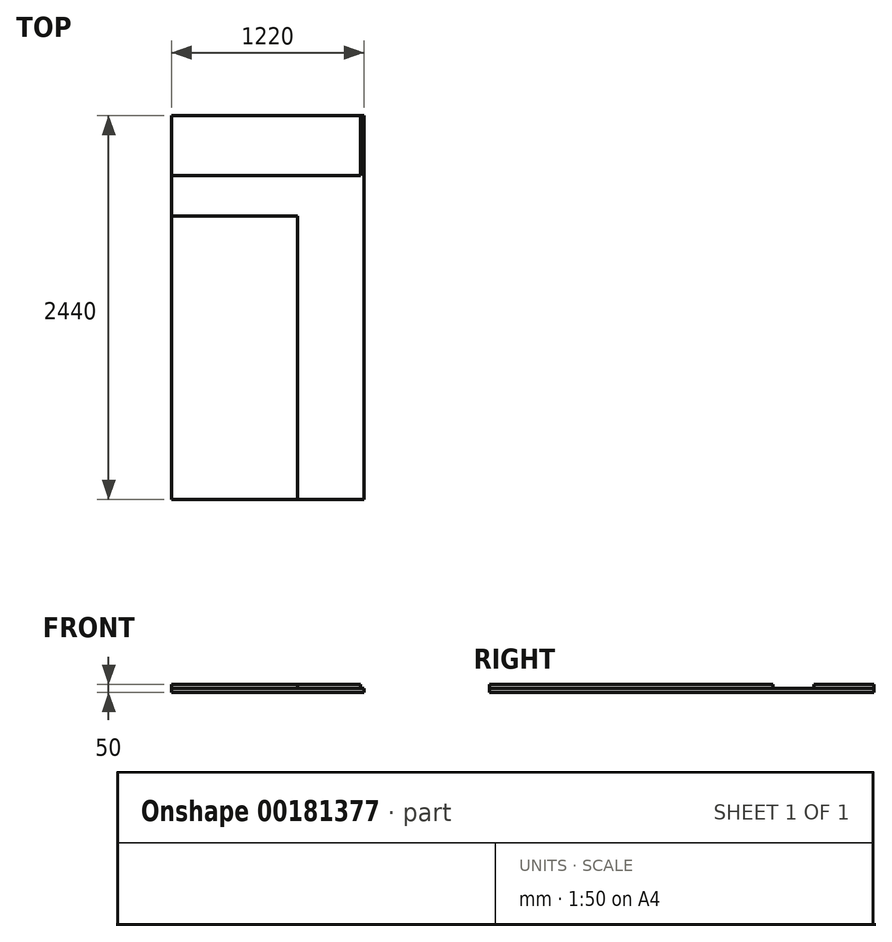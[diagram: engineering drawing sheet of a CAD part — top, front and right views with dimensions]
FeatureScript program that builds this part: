
annotation { "Feature Type Name" : "Feature", "Feature Type Description" : "" }
export const myFeature = defineFeature(function(context is Context, id is Id, definition is map)
    precondition{}
    {
        {
            var Q0;
            Q0=qCreatedBy(makeId("Top.planeOp"),FACE);
            var sketch = newSketch(context, id + "F0", { "sketchPlane" : qUnion([Q0])});
            skPoint(sketch, "E0.middle", {"position": v(0, 0) * mm});
            skLineSegment(sketch, "E1.bottom", {"start": v(-610, -1220) * mm, "end": v(190, -1220) * mm});
            skLineSegment(sketch, "E1.top", {"start": v(-610, 580) * mm, "end": v(190, 580) * mm});
            skLineSegment(sketch, "E1.left", {"start": v(-610, -1220) * mm, "end": v(-610, 580) * mm});
            skLineSegment(sketch, "E1.right", {"start": v(190, -1220) * mm, "end": v(190, 580) * mm});
            skSolve(sketch);
        }
        {
            var Q0;
            Q0 = qSketchRegion(id + "F0", true);
            extrude(context, id + "F1", {"entities" : qUnion([Q0]), "depth" : 25 * mm});
        }
        {
            var Q0;
            Q0=makeQuery(id+"F1.opExtrude","CAP_FACE",FACE,{"disambiguationData":[OSD([sQuery(id+"F0.wireOp",EDGE,"E1.bottom"),sQuery(id+"F0.wireOp",EDGE,"E1.top"),sQuery(id+"F0.wireOp",EDGE,"E1.left"),sQuery(id+"F0.wireOp",EDGE,"E1.right")])],"isStart":true});
            var sketch = newSketch(context, id + "F2", { "sketchPlane" : qUnion([Q0])});
            skLineSegment(sketch, "E2.bottom", {"start": v(-610, -838) * mm, "end": v(590, -838) * mm});
            skLineSegment(sketch, "E2.top", {"start": v(-610, -1220) * mm, "end": v(590, -1220) * mm});
            skLineSegment(sketch, "E2.left", {"start": v(-610, -838) * mm, "end": v(-610, -1220) * mm});
            skLineSegment(sketch, "E2.right", {"start": v(590, -838) * mm, "end": v(590, -1220) * mm});
            skSolve(sketch);
        }
        {
            var Q0;
            Q0 = qSketchRegion(id + "F2", true);
            extrude(context, id + "F3", {"entities" : qUnion([Q0]), "oppositeDirection" : true, "depth" : 25 * mm});
        }
        {
            var Q0;
            Q0=makeQuery(id+"F1.opExtrude","CAP_FACE",FACE,{"disambiguationData":[OSD([sQuery(id+"F0.wireOp",EDGE,"E1.bottom"),sQuery(id+"F0.wireOp",EDGE,"E1.top"),sQuery(id+"F0.wireOp",EDGE,"E1.left"),sQuery(id+"F0.wireOp",EDGE,"E1.right")])],"isStart":true});
            var sketch = newSketch(context, id + "F4", { "sketchPlane" : qUnion([Q0])});
            skLineSegment(sketch, "E3.bottom", {"start": v(-610, 1220) * mm, "end": v(610, 1220) * mm});
            skLineSegment(sketch, "E3.top", {"start": v(-610, -1220) * mm, "end": v(610, -1220) * mm});
            skLineSegment(sketch, "E3.left", {"start": v(-610, 1220) * mm, "end": v(-610, -1220) * mm});
            skLineSegment(sketch, "E3.right", {"start": v(610, 1220) * mm, "end": v(610, -1220) * mm});
            skSolve(sketch);
        }
        {
            var Q0;
            Q0 = qSketchRegion(id + "F4", true);
            extrude(context, id + "F5", {"entities" : qUnion([Q0]), "depth" : 25 * mm});
        }
    });
